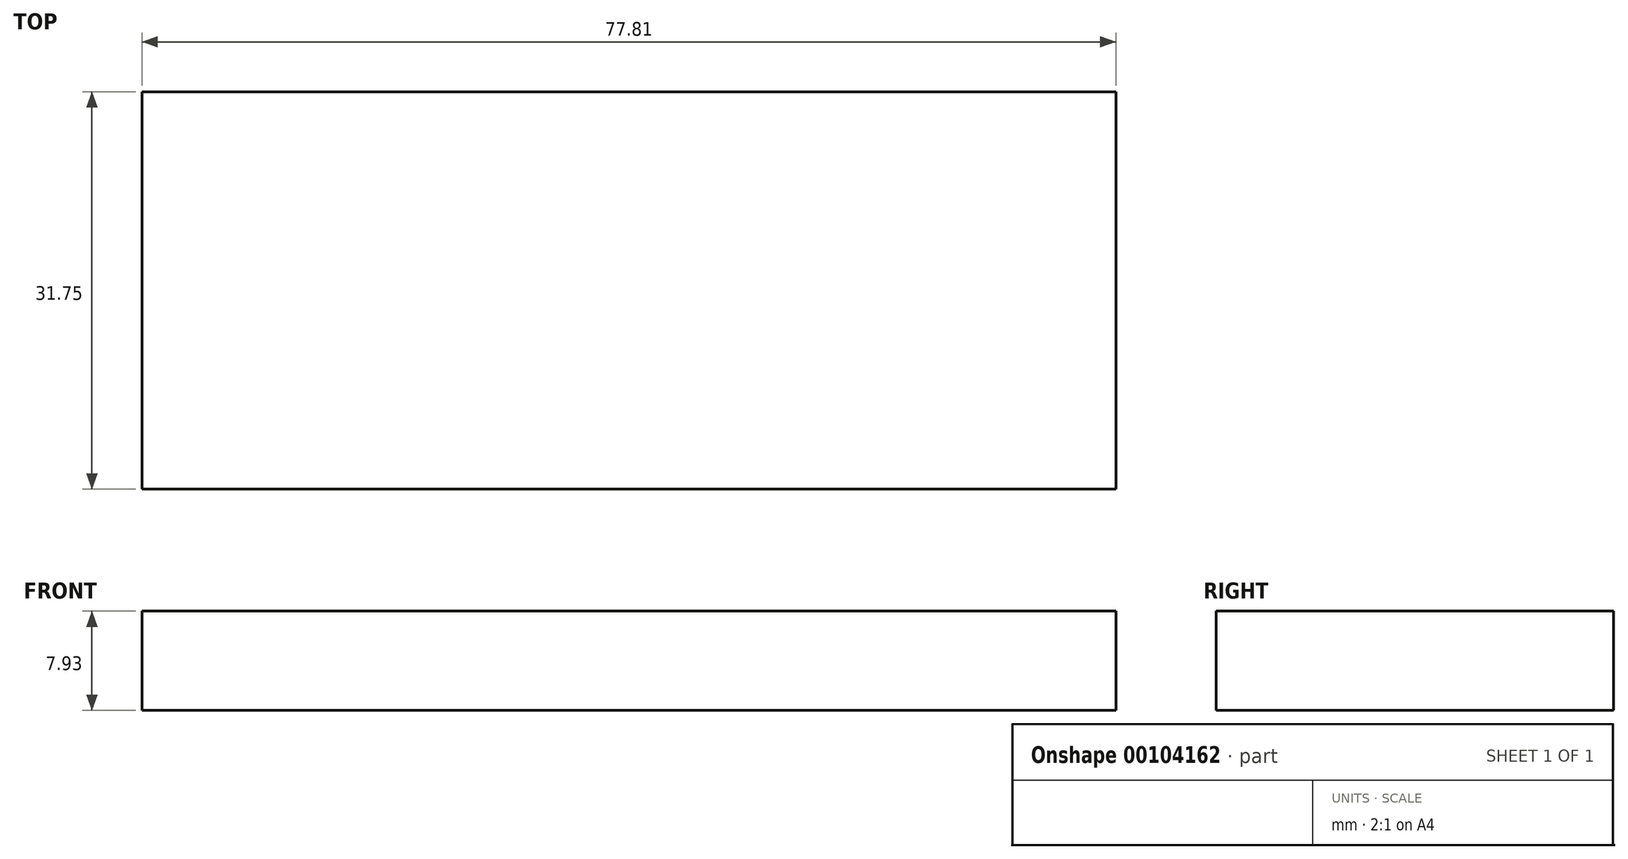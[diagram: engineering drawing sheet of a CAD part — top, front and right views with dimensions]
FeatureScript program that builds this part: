
annotation { "Feature Type Name" : "Feature", "Feature Type Description" : "" }
export const myFeature = defineFeature(function(context is Context, id is Id, definition is map)
    precondition{}
    {
        {
            var Q0;
            Q0=qCreatedBy(makeId("Front.planeOp"),FACE);
            var sketch = newSketch(context, id + "F0", { "sketchPlane" : qUnion([Q0])});
            skLineSegment(sketch, "E0.bottom", {"start": v(-24.02, 2.4) * mm, "end": v(53.79, 2.4) * mm});
            skLineSegment(sketch, "E0.top", {"start": v(-24.02, -5.54) * mm, "end": v(53.79, -5.54) * mm});
            skLineSegment(sketch, "E0.left", {"start": v(-24.02, 2.4) * mm, "end": v(-24.02, -5.54) * mm});
            skLineSegment(sketch, "E0.right", {"start": v(53.79, 2.4) * mm, "end": v(53.79, -5.54) * mm});
            skSolve(sketch);
        }
        {
            var Q0;
            Q0=makeQuery(id+"F0.imprint","IMPRINT",FACE,{"disambiguationData":[TD([[makeQuery(id+"F0.imprint","IMPRINT",EDGE,{"derivedFrom":sQuery(id+"F0.wireOp",EDGE,"E0.bottom")}),-1.0]])]});
            extrude(context, id + "F1", {"entities" : qUnion([Q0]), "depth" : 31.75 * mm});
        }
    });
